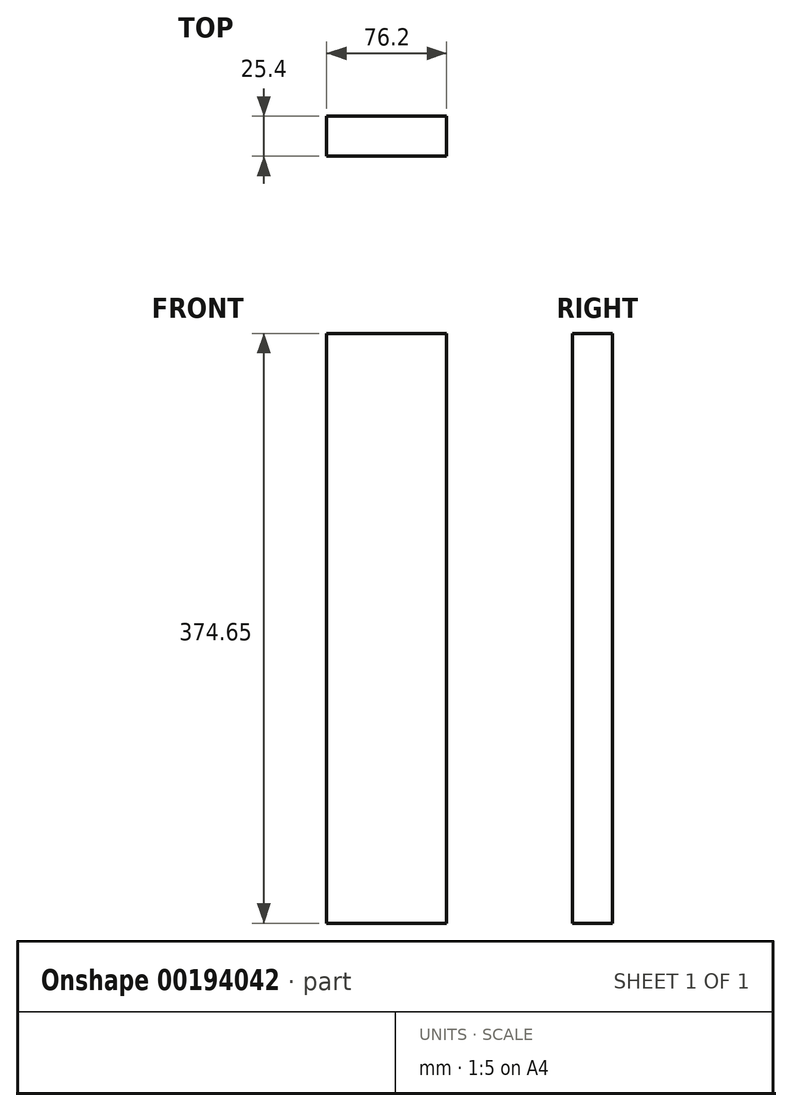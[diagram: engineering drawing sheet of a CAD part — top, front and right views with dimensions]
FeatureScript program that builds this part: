
annotation { "Feature Type Name" : "Feature", "Feature Type Description" : "" }
export const myFeature = defineFeature(function(context is Context, id is Id, definition is map)
    precondition{}
    {
        {
            var Q0;
            Q0=qCreatedBy(makeId("Top.planeOp"),FACE);
            var sketch = newSketch(context, id + "F0", { "sketchPlane" : qUnion([Q0])});
            skLineSegment(sketch, "E0.bottom", {"start": v(38.1, 12.7) * mm, "end": v(-38.1, 12.7) * mm});
            skLineSegment(sketch, "E0.top", {"start": v(38.1, -12.7) * mm, "end": v(-38.1, -12.7) * mm});
            skLineSegment(sketch, "E0.left", {"start": v(38.1, 12.7) * mm, "end": v(38.1, -12.7) * mm});
            skLineSegment(sketch, "E0.right", {"start": v(-38.1, 12.7) * mm, "end": v(-38.1, -12.7) * mm});
            skPoint(sketch, "E0.middle", {"position": v(0, 0) * mm});
            skSolve(sketch);
        }
        {
            var Q0;
            Q0=makeQuery(id+"F0.imprint","IMPRINT",FACE,{"disambiguationData":[TD([[makeQuery(id+"F0.imprint","IMPRINT",EDGE,{"derivedFrom":sQuery(id+"F0.wireOp",EDGE,"E0.bottom")}),1.0]])]});
            extrude(context, id + "F1", {"entities" : qUnion([Q0]), "depth" : 374.65 * mm});
        }
    });
